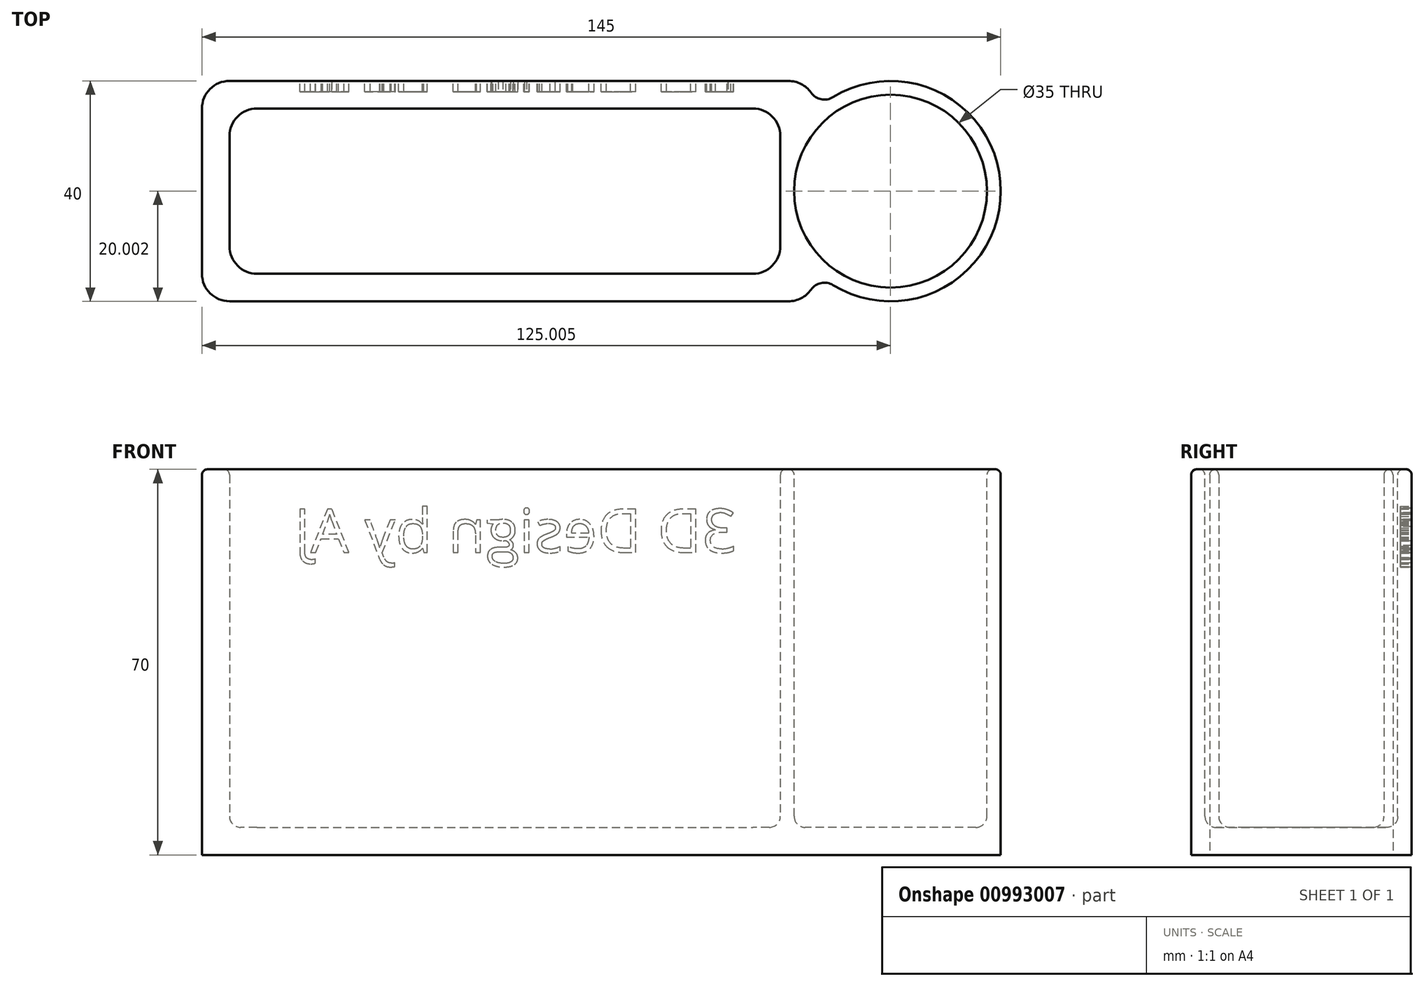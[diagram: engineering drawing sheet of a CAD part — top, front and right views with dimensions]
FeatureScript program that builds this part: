
annotation { "Feature Type Name" : "Feature", "Feature Type Description" : "" }
export const myFeature = defineFeature(function(context is Context, id is Id, definition is map)
    precondition{}
    {
        {
            var Q0;
            Q0=qCreatedBy(makeId("Top.planeOp"),FACE);
            var sketch = newSketch(context, id + "F0", { "sketchPlane" : qUnion([Q0])});
            skLineSegment(sketch, "E0.bottom", {"start": v(-56.23, 57.08) * mm, "end": v(53.77, 57.08) * mm});
            skLineSegment(sketch, "E0.top", {"start": v(-56.23, 17.08) * mm, "end": v(53.77, 17.08) * mm});
            skLineSegment(sketch, "E0.left", {"start": v(-56.23, 57.08) * mm, "end": v(-56.23, 17.08) * mm});
            skLineSegment(sketch, "E0.right", {"start": v(53.77, 57.08) * mm, "end": v(53.77, 17.08) * mm});
            skSolve(sketch);
        }
        {
            var Q0;
            Q0 = qSketchRegion(id + "F0", true);
            extrude(context, id + "F1", {"entities" : qUnion([Q0]), "depth" : 70 * mm, "offsetDistance" : 25 * mm});
        }
        {
            var Q0;
            Q0=makeQuery(id+"F1.opExtrude","CAP_FACE",FACE,{"disambiguationData":[OSD([sQuery(id+"F0.wireOp",EDGE,"E0.bottom"),sQuery(id+"F0.wireOp",EDGE,"E0.top"),sQuery(id+"F0.wireOp",EDGE,"E0.left"),sQuery(id+"F0.wireOp",EDGE,"E0.right")])],"isStart":false});
            shell(context, id + "F2", {"entities" : qUnion([Q0]), "thickness" : 5 * mm});
        }
        {
            var Q0;
            Q0=qCreatedBy(makeId("Top.planeOp"),FACE);
            var sketch = newSketch(context, id + "F3", { "sketchPlane" : qUnion([Q0])});
            skCircle(sketch, "E1", {"center": v(68.77, 37.08) * mm, "radius": 20 * mm});
            skSolve(sketch);
        }
        {
            var Q0;
            Q0=makeQuery(id+"F3.imprint","IMPRINT",FACE,{"disambiguationData":[TD([[makeQuery(id+"F3.imprint","IMPRINT",EDGE,{"derivedFrom":sQuery(id+"F3.wireOp",EDGE,"E1")}),1.0]])]});
            extrude(context, id + "F4", {"entities" : qUnion([Q0]), "operationType" : NewBodyOperationType.ADD, "depth" : 70 * mm, "offsetDistance" : 25 * mm});
        }
        {
            var Q0;
            Q0=makeQuery(id+"F4.boolean.opBoolean","MERGE",FACE,{"derivedFrom":[makeQuery(id+"F1.opExtrude","CAP_FACE",FACE,{"disambiguationData":[OSD([sQuery(id+"F0.wireOp",EDGE,"E0.bottom"),sQuery(id+"F0.wireOp",EDGE,"E0.top"),sQuery(id+"F0.wireOp",EDGE,"E0.left"),sQuery(id+"F0.wireOp",EDGE,"E0.right")])],"isStart":false}),makeQuery(id+"F4.opExtrude","CAP_FACE",FACE,{"disambiguationData":[OSD([sQuery(id+"F3.wireOp",EDGE,"E1")])],"isStart":false})]});
            var sketch = newSketch(context, id + "F5", { "sketchPlane" : qUnion([Q0])});
            skCircle(sketch, "E2", {"center": v(68.77, 37.08) * mm, "radius": 17.5 * mm});
            skSolve(sketch);
        }
        {
            var Q0;
            Q0 = qSketchRegion(id + "F5", true);
            extrude(context, id + "F6", {"entities" : qUnion([Q0]), "operationType" : NewBodyOperationType.REMOVE, "oppositeDirection" : true, "depth" : 65 * mm, "offsetDistance" : 25 * mm});
        }
        {
            var Q0;
            Q0=makeQuery(id+"F4.boolean.opBoolean","INTERSECT",EDGE,{"disambiguationData":[OD(1.0)],"derivedFrom":[makeQuery(id+"F1.opExtrude","SWEPT_FACE",FACE,{"disambiguationData":[OSD([sQuery(id+"F0.wireOp",EDGE,"E0.right")])]}),makeQuery(id+"F4.opExtrude","SWEPT_FACE",FACE,{"disambiguationData":[OSD([sQuery(id+"F3.wireOp",EDGE,"E1")])]})]});
            var Q1;
            Q1=makeQuery(id+"F4.boolean.opBoolean","INTERSECT",EDGE,{"disambiguationData":[OD(0.0)],"derivedFrom":[makeQuery(id+"F1.opExtrude","SWEPT_FACE",FACE,{"disambiguationData":[OSD([sQuery(id+"F0.wireOp",EDGE,"E0.right")])]}),makeQuery(id+"F4.opExtrude","SWEPT_FACE",FACE,{"disambiguationData":[OSD([sQuery(id+"F3.wireOp",EDGE,"E1")])]})]});
            fillet(context, id + "F7", {"entities" : qUnion([Q0, Q1]), "radius" : 3 * mm, "tangentPropagation" : true, "allowEdgeOverflow" : false});
        }
        {
            var Q0;
            Q0=makeQuery(id+"F1.opExtrude","SWEPT_EDGE",EDGE,{"disambiguationData":[OSD([sQuery(id+"F0.wireOp",EDGE,"E0.top"),sQuery(id+"F0.wireOp",EDGE,"E0.right")])]});
            var Q1;
            Q1=makeQuery(id+"F1.opExtrude","SWEPT_EDGE",EDGE,{"disambiguationData":[OSD([sQuery(id+"F0.wireOp",EDGE,"E0.bottom"),sQuery(id+"F0.wireOp",EDGE,"E0.right")])]});
            var Q2;
            Q2=makeQuery(id+"F1.opExtrude","SWEPT_EDGE",EDGE,{"disambiguationData":[OSD([sQuery(id+"F0.wireOp",EDGE,"E0.top"),sQuery(id+"F0.wireOp",EDGE,"E0.left")])]});
            var Q3;
            Q3=makeQuery(id+"F1.opExtrude","SWEPT_EDGE",EDGE,{"disambiguationData":[OSD([sQuery(id+"F0.wireOp",EDGE,"E0.bottom"),sQuery(id+"F0.wireOp",EDGE,"E0.left")])]});
            fillet(context, id + "F8", {"entities" : qUnion([Q0, Q1, Q2, Q3]), "radius" : 5 * mm, "tangentPropagation" : true, "allowEdgeOverflow" : false});
        }
        {
            var Q0;
            Q0=makeQuery(id+"F2.opShell","OFFSET_EDGE",EDGE,{"disambiguationData":[OSD([sQuery(id+"F0.wireOp",EDGE,"E0.bottom"),sQuery(id+"F0.wireOp",EDGE,"E0.right")])]});
            var Q1;
            Q1=makeQuery(id+"F2.opShell","OFFSET_EDGE",EDGE,{"disambiguationData":[OSD([sQuery(id+"F0.wireOp",EDGE,"E0.bottom"),sQuery(id+"F0.wireOp",EDGE,"E0.left")])]});
            var Q2;
            Q2=makeQuery(id+"F2.opShell","OFFSET_EDGE",EDGE,{"disambiguationData":[OSD([sQuery(id+"F0.wireOp",EDGE,"E0.top"),sQuery(id+"F0.wireOp",EDGE,"E0.right")])]});
            var Q3;
            Q3=makeQuery(id+"F2.opShell","OFFSET_EDGE",EDGE,{"disambiguationData":[OSD([sQuery(id+"F0.wireOp",EDGE,"E0.top"),sQuery(id+"F0.wireOp",EDGE,"E0.left")])]});
            fillet(context, id + "F9", {"entities" : qUnion([Q0, Q1, Q2, Q3]), "radius" : 5 * mm, "tangentPropagation" : true, "allowEdgeOverflow" : false});
        }
        {
            var Q0;
            Q0=makeQuery(id+"F4.boolean.opBoolean","MERGE",FACE,{"derivedFrom":[makeQuery(id+"F1.opExtrude","CAP_FACE",FACE,{"disambiguationData":[OSD([sQuery(id+"F0.wireOp",EDGE,"E0.bottom"),sQuery(id+"F0.wireOp",EDGE,"E0.top"),sQuery(id+"F0.wireOp",EDGE,"E0.left"),sQuery(id+"F0.wireOp",EDGE,"E0.right")])],"isStart":false}),makeQuery(id+"F4.opExtrude","CAP_FACE",FACE,{"disambiguationData":[OSD([sQuery(id+"F3.wireOp",EDGE,"E1")])],"isStart":false})]});
            fillet(context, id + "F10", {"entities" : qUnion([Q0]), "radius" : 1 * mm, "tangentPropagation" : true, "allowEdgeOverflow" : false});
        }
        {
            var Q0;
            Q0=makeQuery(id+"F1.opExtrude","SWEPT_FACE",FACE,{"disambiguationData":[OSD([sQuery(id+"F0.wireOp",EDGE,"E0.bottom")])]});
            var sketch = newSketch(context, id + "F11", { "sketchPlane" : qUnion([Q0])});
            skText(sketch, "E3", { "text": "3D Design by AJ", "fontName": "OpenSans-Regular.ttf"});
            const initialGuessF11  = {"E3": [-0.0408, 0.0549, 1, 0, 0.00794]};
            skSetInitialGuess(sketch, initialGuessF11);
            skSolve(sketch);
        }
        {
            var Q0;
            Q0 = qSketchRegion(id + "F11", true);
            extrude(context, id + "F12", {"entities" : qUnion([Q0]), "operationType" : NewBodyOperationType.REMOVE, "oppositeDirection" : true, "depth" : 2 * mm, "offsetDistance" : 25 * mm});
        }
        {
            var Q0;
            Q0=makeQuery(id+"F2.opShell","OFFSET_FACE",FACE,{"disambiguationData":[OSD([sQuery(id+"F0.wireOp",EDGE,"E0.bottom"),sQuery(id+"F0.wireOp",EDGE,"E0.top"),sQuery(id+"F0.wireOp",EDGE,"E0.left"),sQuery(id+"F0.wireOp",EDGE,"E0.right")])]});
            fillet(context, id + "F13", {"entities" : qUnion([Q0]), "radius" : 2 * mm, "tangentPropagation" : true, "allowEdgeOverflow" : false});
        }
        {
            var Q0;
            Q0=makeQuery(id+"F6.boolean.opBoolean","COPY",FACE,{"derivedFrom":makeQuery(id+"F6.opExtrude","CAP_FACE",FACE,{"disambiguationData":[OSD([sQuery(id+"F5.wireOp",EDGE,"E2")])],"isStart":false})});
            fillet(context, id + "F14", {"entities" : qUnion([Q0]), "radius" : 2 * mm, "tangentPropagation" : true, "allowEdgeOverflow" : false});
        }
    });
